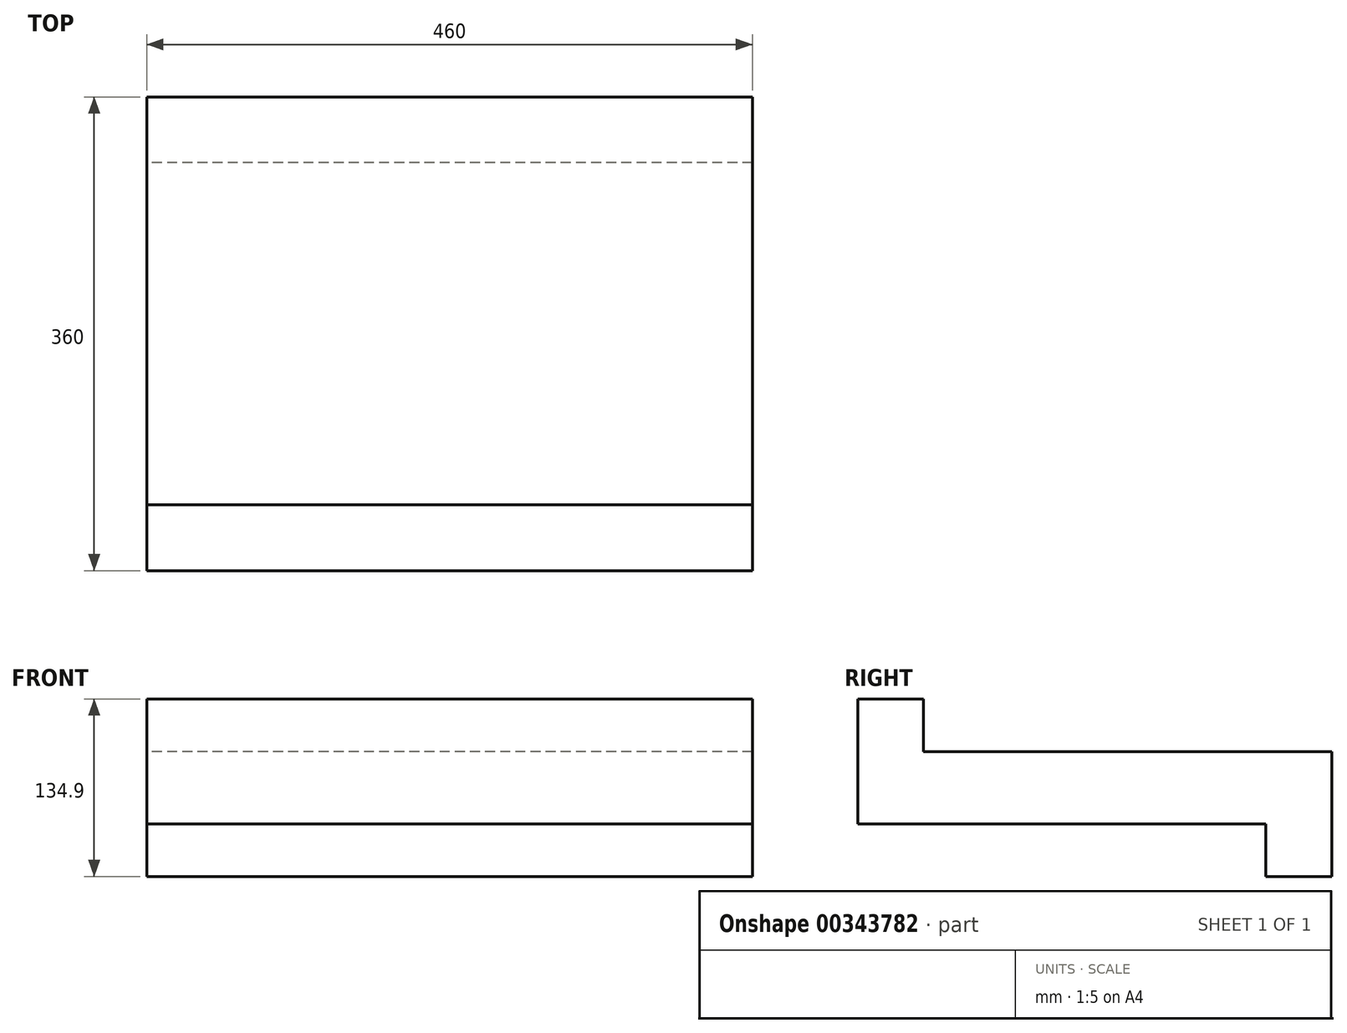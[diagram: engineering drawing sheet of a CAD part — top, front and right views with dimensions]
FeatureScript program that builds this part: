
annotation { "Feature Type Name" : "Feature", "Feature Type Description" : "" }
export const myFeature = defineFeature(function(context is Context, id is Id, definition is map)
    precondition{}
    {
        {
            var Q0;
            Q0=qCreatedBy(makeId("Right.planeOp"),FACE);
            var sketch = newSketch(context, id + "F0", { "sketchPlane" : qUnion([Q0])});
            skLineSegment(sketch, "E0", {"start": v(-180, -27.45) * mm, "end": v(130, -27.45) * mm});
            skLineSegment(sketch, "E1", {"start": v(130, -27.45) * mm, "end": v(130, -67.45) * mm});
            skLineSegment(sketch, "E2", {"start": v(130, -67.45) * mm, "end": v(180, -67.45) * mm});
            skLineSegment(sketch, "E3", {"start": v(180, -67.45) * mm, "end": v(180, 27.45) * mm});
            skLineSegment(sketch, "E4", {"start": v(180, 27.45) * mm, "end": v(-130, 27.45) * mm});
            skLineSegment(sketch, "E5", {"start": v(-130, 27.45) * mm, "end": v(-130, 67.45) * mm});
            skLineSegment(sketch, "E6", {"start": v(-130, 67.45) * mm, "end": v(-180, 67.45) * mm});
            skLineSegment(sketch, "E7", {"start": v(-180, 67.45) * mm, "end": v(-180, -27.45) * mm});
            skSolve(sketch);
        }
        {
            var Q0;
            Q0=makeQuery(id+"F0.imprint","IMPRINT",FACE,{"disambiguationData":[TD([[makeQuery(id+"F0.imprint","IMPRINT",EDGE,{"derivedFrom":sQuery(id+"F0.wireOp",EDGE,"E0")}),1.0]])]});
            extrude(context, id + "F1", {"entities" : qUnion([Q0]), "depth" : 460 * mm});
        }
    });
